# Revit family: 2059797 Sylvania Lighting Fixture BEACON MUSE Xicato 3K O B DIM LS3 White
name_source: partatom
category: Lighting Fixtures
revit_build: Autodesk Revit 2016 (Build: 20150220_1215(x64)
units: mm (PartAtom-declared; Revit-internal decimal feet)

## family parameters
Cut with Voids When Loaded = No
Host = Face
Light Source = Yes
OmniClass Number = 23.80.70.00
OmniClass Title = Lighting
Part Type = Normal
Room Calculation Point = No
Round Connector Dimension = Use Diameter
Shared = No

## types (1)
- 2059797 BEACON MUSE XICATO 3K O/B DIM LS3 WHT
    Adaptor Inside Width = 17 mm
    Adaptor Pivot = 25 mm  [stored 0.082021 ft]
    Adaptor Width = 35 mm
    Apparent Load = 20 VA
    Assembly Code = D5020200
    AssetType = Fixed
    ClassificationName = Uniclass2015
    ClassificationValue = EF_70_80
    Color Filter = 16777215
    Cost = 0 $
    Default Elevation = 115 mm
    Description = Integrated LED spotlight with Xicato Artist LED Module, white RAL 9016, unique soft-touch ring, adjustable beam angle from a 8° spot to a 55° flood, compact and minimalist design, ideal for museum, gallery and high-end retail applications, die-cast aluminium body, passive cooling heatsink, beam angle: 8° spot to 52° flood, optics: aspheric glass lens, colour temperature: 3000K warm white, total system power: 20W, total fixture output: 338/598lm, luminaire efficacy: 30lm/W, LOR: 100%, colour rendering: Ra 97 typical, LED Chromacity: 3 step MacAdam ellipse, lifetime: >50,000 hours at L70B50, energy class: A++, A+, A, IR/UV free light source without heat radiation, operating voltage: 220-240V / 50-60Hz, drive current: 700mA, electronic driver, dimmable via on-board potentiometer, power factor: 0.9 electrical protection: CLASS II, 3-circuit track adaptor, suitable for Concord Lytespan 3 track, ingress protection rating: IP20, suitable for internal environment only, horizontal rotation: 355°, vertical tilt: 90°, dimensions: Ø80x135x176mm, weight: 0.95kg
    Diameter = 80 mm  [stored 0.262467 ft]
    Dimming Lamp Color Temperature Shift = <None>
    DocumentationLiterature = http://www.sylvania-lighting.com
    Driver Width = 85 mm
    DurationUnit = hours
    Emit Shape Visible in Rendering = No
    Emit from Circle Diameter = 610 mm
    ExpectedLife = 50000
    IfcExportAs = 30
    IfcExportType = IfcLightFixtureType
    ImpactProtectionIndex = Class II
    InputNominalFrequency = IK02
    InputVoltage = IP20
    Keynote = 0
    LampMacAdamStep = 16500
    LampNominalLuminous = LED
    Light = <By Category>
    LightOutputRatio = 3
    Lighting Material = <By Category>
    LuminaireType = 338/598 lm
    LuminousEfficacy = 100
    Material_1_FEILO = <By Category>
    Material_2_FEILO = <By Category>
    Material_3_FEILO = <By Category>
    Material_4_FEILO = <By Category>
    Model = BEACON MUSE Xicato 3K O/B DIM LS3 White
    ModelNumber = 2059797
    ModelReference = BEACON MUSE Xicato 3K O/B DIM LS3 White
    Name = BEACON MUSE Xicato 3K O/B DIM LS3 White
    NominalDepth = 0 mm  [stored 0 ft]
    NominalHeight = 0 mm  [stored 0 ft]
    NominalLength = 0 mm  [stored 0 ft]
    Photometric Web File = 2059797.ies
    PowerConsumption = 0
    PowerFactor = 0
    Tilt Angle = 90.00°
    Type Image = <None>
    TypeName = BEACON MUSE Xicato 3K O/B DIM LS3 White
    URL = 2059797.ies
    Voltage = 0 V
    WarrantyDescription = 0.95
    WarrantyDurationUnit = http://www.sylvania-lighting.com
    ceiling drop = 180 mm
    driver head distance = 15 mm  [stored 0.0492126 ft]
    head from driver = 52 mm

note: [stored X ft] marks values corroborated as IEEE doubles in the binary element streams (Revit-internal decimal feet)

## geometry (parser evidence)
native form markers: Sweep x3
no freeform markers — native parametric forms only
